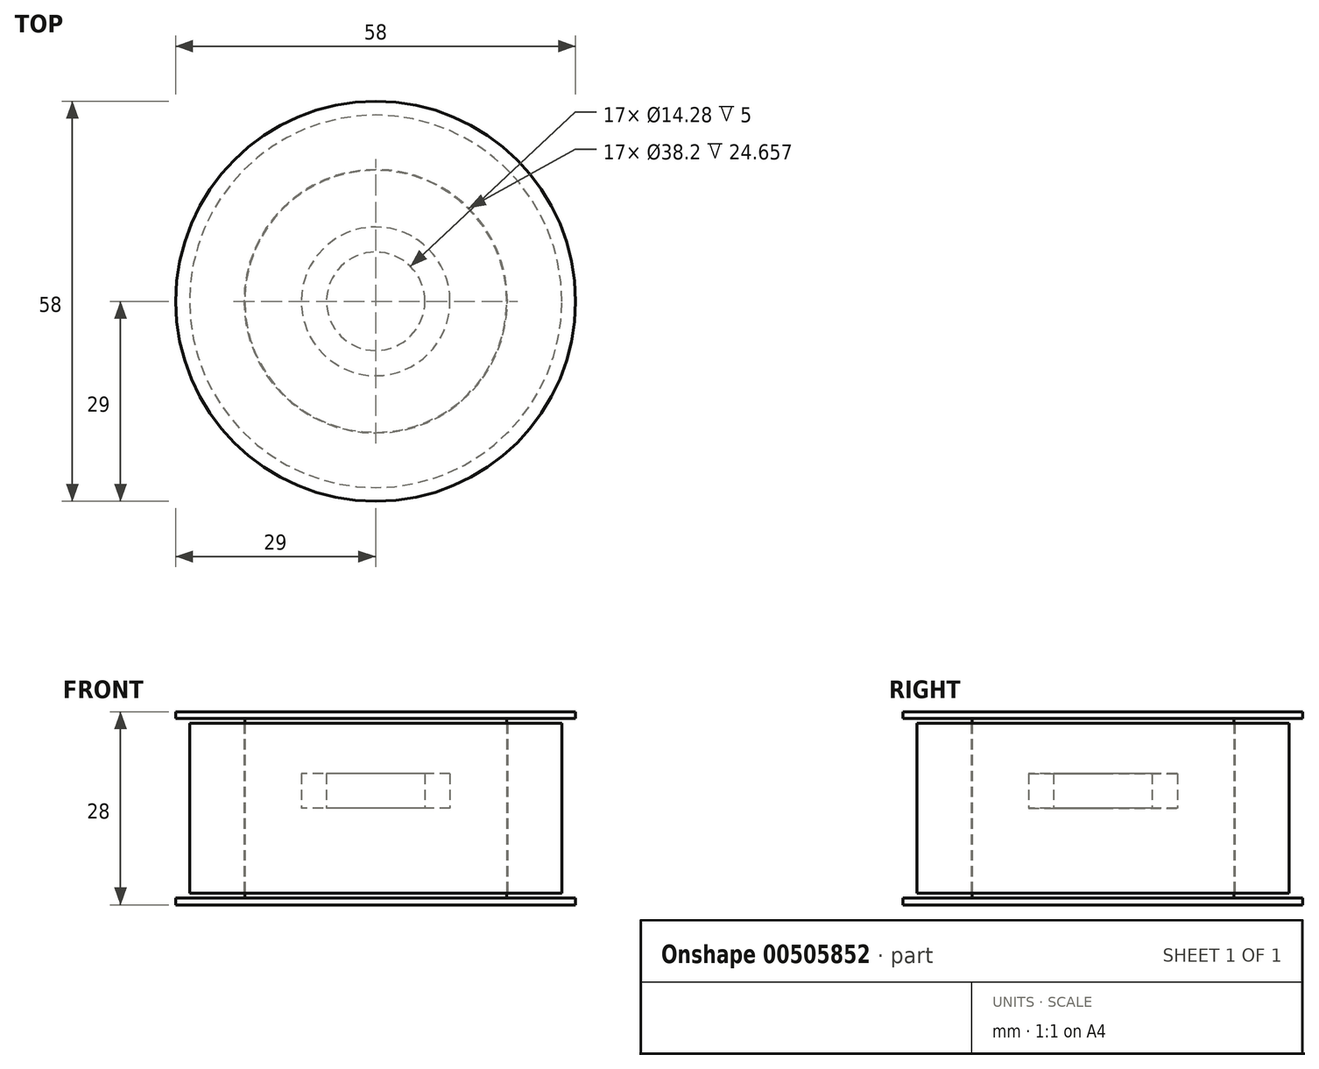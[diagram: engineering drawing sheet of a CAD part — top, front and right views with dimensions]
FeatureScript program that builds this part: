
annotation { "Feature Type Name" : "Feature", "Feature Type Description" : "" }
export const myFeature = defineFeature(function(context is Context, id is Id, definition is map)
    precondition{}
    {
        {
            var Q0;
            Q0=qCreatedBy(makeId("Top.planeOp"),FACE);
            var sketch = newSketch(context, id + "F0", { "sketchPlane" : qUnion([Q0])});
            skCircle(sketch, "E0", {"center": v(0, 0) * mm, "radius": 10.78 * mm});
            skCircle(sketch, "E1", {"center": v(0, 0) * mm, "radius": 7.14 * mm});
            skSolve(sketch);
        }
        {
            var Q0;
            Q0 = qSketchRegion(id + "F0", true);
            extrude(context, id + "F1", {"entities" : qUnion([Q0]), "depth" : 5 * mm, "offsetDistance" : 25 * mm});
        }
        {
            var Q0;
            Q0=qCreatedBy(makeId("Right.planeOp"),FACE);
            var sketch = newSketch(context, id + "F2", { "sketchPlane" : qUnion([Q0])});
            skLineSegment(sketch, "E2", {"start": v(0, 0) * mm, "end": v(0, 43.8) * mm, "construction": true});
            skLineSegment(sketch, "E3", {"start": v(0, 14) * mm, "end": v(-29, 14) * mm});
            skLineSegment(sketch, "E4", {"start": v(-29, 14) * mm, "end": v(-29, 13) * mm});
            skLineSegment(sketch, "E5", {"start": v(-29, 13) * mm, "end": v(-19, 13) * mm});
            skLineSegment(sketch, "E6", {"start": v(0, 0) * mm, "end": v(-34.72, 0) * mm, "construction": true});
            skLineSegment(sketch, "E7.MirrorCS", {"start": v(-29, -13) * mm, "end": v(-19, -13) * mm});
            skLineSegment(sketch, "E8.MirrorCS", {"start": v(0, -14) * mm, "end": v(-29, -14) * mm});
            skLineSegment(sketch, "E9.MirrorCS", {"start": v(-29, -14) * mm, "end": v(-29, -13) * mm});
            skLineSegment(sketch, "E10", {"start": v(-19, 13) * mm, "end": v(-19, -13) * mm});
            skLineSegment(sketch, "E11", {"start": v(0, 14) * mm, "end": v(0, -14) * mm});
            skLineSegment(sketch, "E12.bottom", {"start": v(-27, 12.33) * mm, "end": v(-19.1, 12.33) * mm});
            skLineSegment(sketch, "E12.top", {"start": v(-27, -12.33) * mm, "end": v(-19.1, -12.33) * mm});
            skLineSegment(sketch, "E12.left", {"start": v(-27, 12.33) * mm, "end": v(-27, -12.33) * mm});
            skLineSegment(sketch, "E12.right", {"start": v(-19.1, 12.33) * mm, "end": v(-19.1, -12.33) * mm});
            skPoint(sketch, "E12.middle", {"position": v(-23.05, 0) * mm});
            skSolve(sketch);
        }
        {
            var Q0;
            Q0=makeQuery(id+"F2.imprint","IMPRINT",FACE,{"disambiguationData":[TD([[makeQuery(id+"F2.imprint","IMPRINT",EDGE,{"derivedFrom":sQuery(id+"F2.wireOp",EDGE,"E3")}),1.0]])]});
            var Q1;
            Q1=makeQuery(id+"F2.imprint","IMPRINT",FACE,{"disambiguationData":[TD([[makeQuery(id+"F2.imprint","IMPRINT",EDGE,{"derivedFrom":sQuery(id+"F2.wireOp",EDGE,"E12.bottom")}),-1.0]])]});
            var Q2;
            Q2=sQuery(id+"F2.wireOp",EDGE,"E2");
            revolve(context, id + "F3", {"entities" : qUnion([Q0, Q1]), "axis" : qUnion([Q2]), "revolveType" : RevolveType.FULL});
        }
    });
